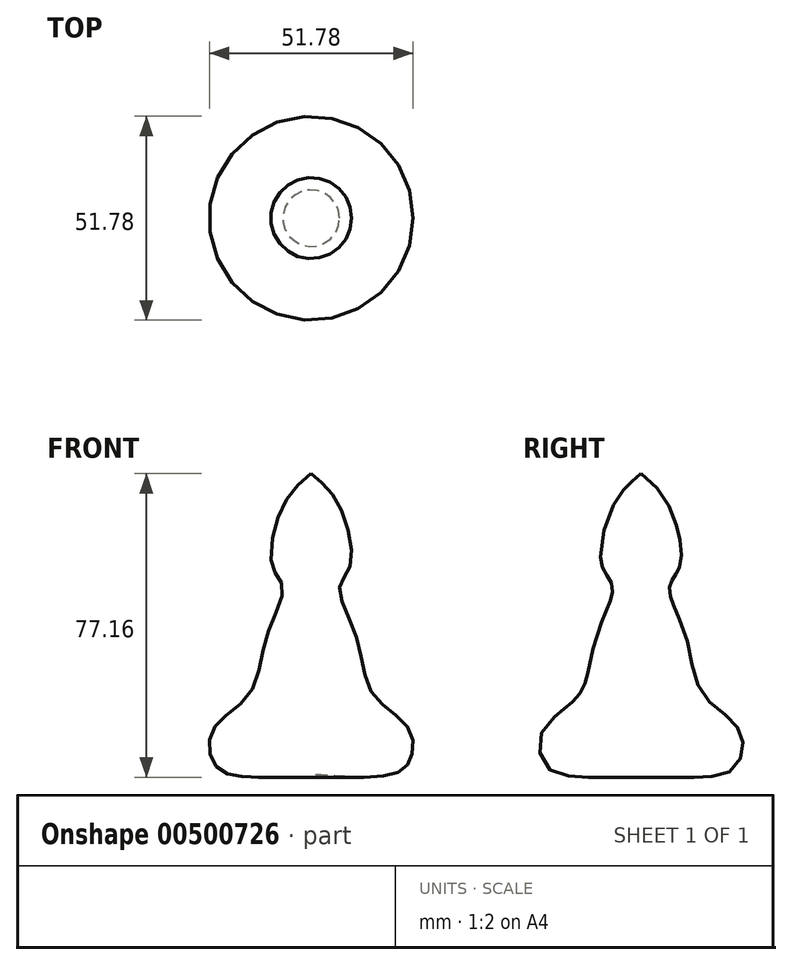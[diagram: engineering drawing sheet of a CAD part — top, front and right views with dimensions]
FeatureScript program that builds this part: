
annotation { "Feature Type Name" : "Feature", "Feature Type Description" : "" }
export const myFeature = defineFeature(function(context is Context, id is Id, definition is map)
    precondition{}
    {
        {
            var Q0;
            Q0=qCreatedBy(makeId("Front.planeOp"),FACE);
            var sketch = newSketch(context, id + "F0", { "sketchPlane" : qUnion([Q0])});
            skLineSegment(sketch, "E0", {"start": v(0, 0) * mm, "end": v(0, 76.4) * mm});
            skFitSpline(sketch, "E1", {"points": [v(0, 76.4) * mm, v(6.92, 68.58) * mm, v(9.93, 52.94) * mm, v(7.22, 47.52) * mm, v(11.43, 34.9) * mm, v(15.64, 20.45) * mm, v(24.66, 11.73) * mm, v(25.27, 3.91) * mm, v(20.75, 0) * mm, v(0, 0) * mm], "startDerivative": vector(70.05, -57.96) * mm, "endDerivative": vector(-163.72, 13.16) * mm});
            skSolve(sketch);
        }
        {
            var Q0;
            Q0 = qSketchRegion(id + "F0", true);
            var Q1;
            Q1=sQuery(id+"F0.wireOp",EDGE,"E0");
            revolve(context, id + "F1", {"entities" : qUnion([Q0]), "axis" : qUnion([Q1]), "revolveType" : RevolveType.FULL});
        }
        {
            var Q0;
            Q0=makeQuery(id+"F1.opRevolve","SWEPT_BODY",BODY,{"disambiguationData":[OSD([sQuery(id+"F0.wireOp",EDGE,"E0"),sQuery(id+"F0.wireOp",EDGE,"E1")])]});
            transform(context, id + "F2", {"entities" : qUnion([Q0]), "transformType" : TransformType.TRANSLATION_3D, "dx" : 50.8 * mm, "dy" : 50.8 * mm, "dz" : 0 * mm, "makeCopy" : false});
        }
    });
